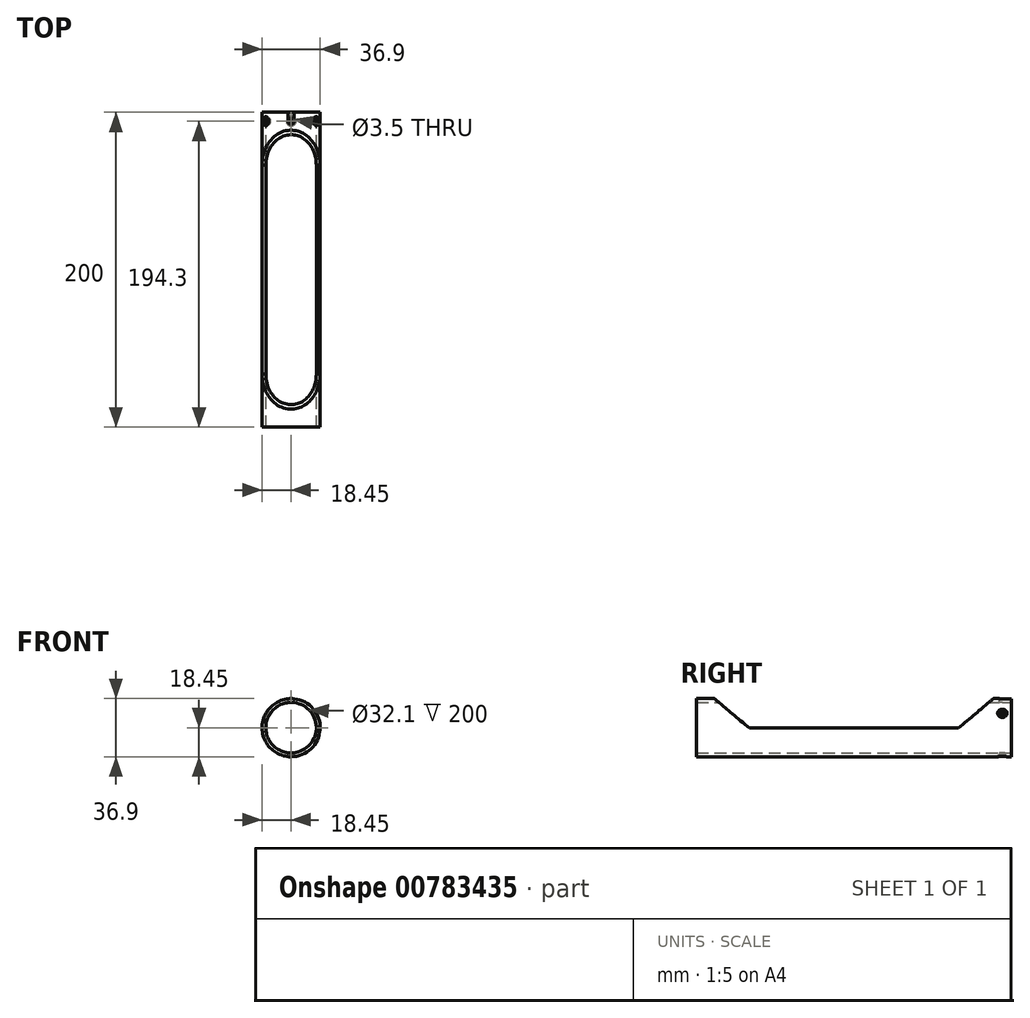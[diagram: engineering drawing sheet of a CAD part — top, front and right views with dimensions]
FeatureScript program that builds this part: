
annotation { "Feature Type Name" : "Feature", "Feature Type Description" : "" }
export const myFeature = defineFeature(function(context is Context, id is Id, definition is map)
    precondition{}
    {
        {
            var Q0;
            Q0=qCreatedBy(makeId("Front.planeOp"),FACE);
            var sketch = newSketch(context, id + "F0", { "sketchPlane" : qUnion([Q0])});
            skCircle(sketch, "E0", {"center": v(0, 0) * mm, "radius": 18.45 * mm});
            skCircle(sketch, "E1", {"center": v(0, 0) * mm, "radius": 16.05 * mm});
            skLineSegment(sketch, "E2.bottom", {"start": v(18.45, -18.45) * mm, "end": v(-18.45, -18.45) * mm});
            skLineSegment(sketch, "E2.top", {"start": v(18.45, 18.45) * mm, "end": v(-18.45, 18.45) * mm});
            skLineSegment(sketch, "E2.left", {"start": v(18.45, -18.45) * mm, "end": v(18.45, 18.45) * mm});
            skLineSegment(sketch, "E2.right", {"start": v(-18.45, -18.45) * mm, "end": v(-18.45, 18.45) * mm});
            skLineSegment(sketch, "E3", {"start": v(0, 0) * mm, "end": v(0, 18.45) * mm});
            skLineSegment(sketch, "E4", {"start": v(0, 0) * mm, "end": v(0, -18.45) * mm});
            skLineSegment(sketch, "E5", {"start": v(0, 0) * mm, "end": v(-15.98, 9.22) * mm});
            skLineSegment(sketch, "E6", {"start": v(0, 0) * mm, "end": v(15.98, 9.23) * mm});
            skSolve(sketch);
        }
        {
            var Q0;
            {var subQ3=sQuery(id+"F0.wireOp",EDGE,"CAZaTLFN-tJie-LHG7-8vTy-squ8jarRoMMn");var subQ5=sQuery(id+"F0.wireOp",EDGE,"E1");var subQ6=makeQuery(id+"F0.imprint","INTERSECT",VERTEX,{"derivedFrom":[subQ5,subQ3]});Q0=makeQuery(id+"F0.imprint","IMPRINT",FACE,{"disambiguationData":[TD([[makeQuery(id+"F0.imprint","IMPRINT",EDGE,{"disambiguationData":[TD([[subQ6,1.0]])],"derivedFrom":subQ5}),-1.0]])]});}
            var Q1;
            {var subQ3=sQuery(id+"F0.wireOp",EDGE,"CAZaTLFN-tJie-LHG7-8vTy-squ8jarRoMMn");var subQ5=sQuery(id+"F0.wireOp",EDGE,"E1");var subQ6=makeQuery(id+"F0.imprint","INTERSECT",VERTEX,{"derivedFrom":[subQ5,subQ3]});Q1=makeQuery(id+"F0.imprint","IMPRINT",FACE,{"disambiguationData":[TD([[makeQuery(id+"F0.imprint","IMPRINT",EDGE,{"disambiguationData":[TD([[subQ6,-1.0]])],"derivedFrom":subQ5}),-1.0]])]});}
            var Q2;
            {var subQ0=sQuery(id+"F0.wireOp",EDGE,"l8s0sOfb-fzFU-R0BE-n0NO-c75pVUIZOnGM");var subQ1=sQuery(id+"F0.wireOp",EDGE,"E0");var subQ2=makeQuery(id+"F0.imprint","INTERSECT",VERTEX,{"derivedFrom":[subQ1,subQ0]});Q2=makeQuery(id+"F0.imprint","IMPRINT",FACE,{"disambiguationData":[TD([[makeQuery(id+"F0.imprint","IMPRINT",EDGE,{"disambiguationData":[TD([[subQ2,1.0]])],"derivedFrom":subQ1}),1.0]])]});}
            var Q3;
            {var subQ0=sQuery(id+"F0.wireOp",EDGE,"4xxhsBqu-Dr4I-gKWc-ZI2R-gIkBFB4eemaq");var subQ1=sQuery(id+"F0.wireOp",EDGE,"E0");var subQ2=makeQuery(id+"F0.imprint","INTERSECT",VERTEX,{"derivedFrom":[subQ1,subQ0]});Q3=makeQuery(id+"F0.imprint","IMPRINT",FACE,{"disambiguationData":[TD([[makeQuery(id+"F0.imprint","IMPRINT",EDGE,{"disambiguationData":[TD([[subQ2,-1.0]])],"derivedFrom":subQ1}),1.0]])]});}
            var Q4;
            Q4=sQuery(id+"F0.wireOp",EDGE,"E0");
            extrude(context, id + "F1", {"entities" : qUnion([Q0, Q1, Q2, Q3]), "surfaceEntities" : qUnion([Q4]), "depth" : 100 * mm, "offsetDistance" : 25.4 * mm, "hasSecondDirection" : true, "secondDirectionOppositeDirection" : true, "secondDirectionDepth" : 100 * mm});
        }
        {
            var Q0;
            Q0=qCreatedBy(makeId("Right.planeOp"),FACE);
            var sketch = newSketch(context, id + "F2", { "sketchPlane" : qUnion([Q0])});
            skLineSegment(sketch, "E7.bottom", {"start": v(88.6, -0.25) * mm, "end": v(-88.6, -0.25) * mm});
            skLineSegment(sketch, "E7.top", {"start": v(88.6, 37.15) * mm, "end": v(-88.6, 37.15) * mm});
            skLineSegment(sketch, "E7.left", {"start": v(88.6, -0.25) * mm, "end": v(88.6, 37.15) * mm});
            skLineSegment(sketch, "E7.right", {"start": v(-88.6, -0.25) * mm, "end": v(-88.6, 37.15) * mm});
            skPoint(sketch, "E7.middle", {"position": v(0, 18.45) * mm});
            skLineSegment(sketch, "E8", {"start": v(-100, 18.45) * mm, "end": v(100, 18.45) * mm});
            skLineSegment(sketch, "E9", {"start": v(100, -18.45) * mm, "end": v(-100, -18.45) * mm});
            skLineSegment(sketch, "E10", {"start": v(88.6, 18.45) * mm, "end": v(66.31, -0.25) * mm});
            skLineSegment(sketch, "E11.MirrorCS", {"start": v(-88.6, 18.45) * mm, "end": v(-66.31, -0.25) * mm});
            skSolve(sketch);
        }
        {
            var Q0;
            {var subQ0=sQuery(id+"F2.wireOp",EDGE,"E7.top");Q0=makeQuery(id+"F2.imprint","IMPRINT",FACE,{"disambiguationData":[TD([[makeQuery(id+"F2.imprint","IMPRINT",EDGE,{"derivedFrom":subQ0}),1.0]])]});}
            var Q1;
            {var subQ0=sQuery(id+"F2.wireOp",EDGE,"E10");Q1=makeQuery(id+"F2.imprint","IMPRINT",FACE,{"disambiguationData":[TD([[makeQuery(id+"F2.imprint","IMPRINT",EDGE,{"derivedFrom":subQ0}),-1.0]])]});}
            extrude(context, id + "F3", {"entities" : qUnion([Q0, Q1]), "operationType" : NewBodyOperationType.REMOVE, "oppositeDirection" : true, "depth" : 50.8 * mm, "offsetDistance" : 25.4 * mm, "hasSecondDirection" : true, "secondDirectionOppositeDirection" : false, "secondDirectionDepth" : 50.8 * mm});
        }
        {
            var Q0;
            Q0=sQuery(id+"F0.wireOp",VERTEX,"E5.end");
            var Q1;
            Q1=sQuery(id+"F0.wireOp",EDGE,"E5");
            cPlane(context, id + "F4", {"entities" : qUnion([Q0, Q1]), "cplaneType" : CPlaneType.CURVE_POINT, "offset" : 25 * mm, "width" : 150 * mm, "height" : 150 * mm});
        }
        {
            var Q0;
            Q0=qCreatedBy(id+"F4.planeOp",FACE);
            var sketch = newSketch(context, id + "F5", { "sketchPlane" : qUnion([Q0])});
            skPoint(sketch, "E12", {"position": v(-94.3, 0) * mm});
            skPoint(sketch, "E13.MirrorP", {"position": v(94.3, 0) * mm});
            skSolve(sketch);
        }
        {
            var Q0;
            Q0=sQuery(id+"F5.wireOp",VERTEX,"E12");
            var Q1;
            Q1=makeQuery(id+"F1.opExtrude","SWEPT_BODY",BODY,{"disambiguationData":[OSD([sQuery(id+"F0.wireOp",EDGE,"E0"),sQuery(id+"F0.wireOp",EDGE,"E1")])]});
            hole(context, id + "F6", {"style" : HoleStyle.C_SINK, "endStyle" : HoleEndStyle.BLIND, "holeDiameter" : 3.5 * mm, "cSinkDiameter" : 6 * mm, "cSinkAngle" : 100 * degree, "majorDiameter" : 5 * mm, "holeDepth" : 5 * mm, "isTappedThrough" : true, "tappedDepth" : 12 * mm, "tapClearance" : 3, "locations" : qUnion([Q0]), "scope" : qUnion([Q1])});
        }
        {
            var Q0;
            Q0=sQuery(id+"F0.wireOp",VERTEX,"E6.end");
            var Q1;
            Q1=sQuery(id+"F0.wireOp",EDGE,"E6");
            cPlane(context, id + "F7", {"entities" : qUnion([Q0, Q1]), "cplaneType" : CPlaneType.CURVE_POINT, "offset" : 25 * mm, "width" : 150 * mm, "height" : 150 * mm});
        }
        {
            var Q0;
            Q0=qCreatedBy(id+"F7.planeOp",FACE);
            var sketch = newSketch(context, id + "F8", { "sketchPlane" : qUnion([Q0])});
            skPoint(sketch, "E14", {"position": v(94.3, 0) * mm});
            skSolve(sketch);
        }
        {
            var Q0;
            Q0=sQuery(id+"F8.wireOp",VERTEX,"E14");
            var Q1;
            Q1=makeQuery(id+"F1.opExtrude","SWEPT_BODY",BODY,{"disambiguationData":[OSD([sQuery(id+"F0.wireOp",EDGE,"E0"),sQuery(id+"F0.wireOp",EDGE,"E1")])]});
            hole(context, id + "F9", {"style" : HoleStyle.C_SINK, "endStyle" : HoleEndStyle.BLIND, "holeDiameter" : 3.5 * mm, "cSinkDiameter" : 6 * mm, "cSinkAngle" : 100 * degree, "majorDiameter" : 5 * mm, "holeDepth" : 5 * mm, "isTappedThrough" : true, "tappedDepth" : 12 * mm, "tapClearance" : 3, "locations" : qUnion([Q0]), "scope" : qUnion([Q1])});
        }
        {
            var Q0;
            Q0=sQuery(id+"F0.wireOp",VERTEX,"E3.end");
            var Q1;
            Q1=sQuery(id+"F0.wireOp",EDGE,"E3");
            cPlane(context, id + "F10", {"entities" : qUnion([Q0, Q1]), "cplaneType" : CPlaneType.CURVE_POINT, "offset" : 25 * mm, "width" : 150 * mm, "height" : 150 * mm});
        }
        {
            var Q0;
            Q0=qCreatedBy(id+"F10.planeOp",FACE);
            var sketch = newSketch(context, id + "F11", { "sketchPlane" : qUnion([Q0])});
            skCircle(sketch, "E15", {"center": v(0, 94.3) * mm, "radius": 2 * mm});
            skLineSegment(sketch, "E16", {"start": v(2, 94.3) * mm, "end": v(2, 100) * mm});
            skLineSegment(sketch, "E17", {"start": v(-2, 94.3) * mm, "end": v(-2, 100) * mm});
            skLineSegment(sketch, "E18", {"start": v(-2, 100) * mm, "end": v(2, 100) * mm});
            skLineSegment(sketch, "E19.0", {"start": v(18.45, 100) * mm, "end": v(-18.45, 100) * mm});
            skSolve(sketch);
        }
        {
            var Q0;
            {var subQ0=sQuery(id+"F11.wireOp",EDGE,"E16");Q0=makeQuery(id+"F11.imprint","IMPRINT",FACE,{"disambiguationData":[TD([[makeQuery(id+"F11.imprint","IMPRINT",EDGE,{"derivedFrom":subQ0}),1.0]])]});}
            var Q1;
            {var subQ0=sQuery(id+"F11.wireOp",EDGE,"E15");var subQ1=makeQuery(id+"F11.imprint","INTERSECT",VERTEX,{"derivedFrom":[subQ0,sQuery(id+"F11.wireOp",EDGE,"E16")]});Q1=makeQuery(id+"F11.imprint","IMPRINT",FACE,{"disambiguationData":[TD([[makeQuery(id+"F11.imprint","IMPRINT",EDGE,{"disambiguationData":[TD([[subQ1,-1.0]])],"derivedFrom":subQ0}),1.0]])]});}
            extrude(context, id + "F12", {"entities" : qUnion([Q0, Q1]), "operationType" : NewBodyOperationType.REMOVE, "oppositeDirection" : true, "depth" : 19.1 * mm, "offsetDistance" : 25 * mm});
        }
        {
            var Q0;
            Q0=sQuery(id+"F0.wireOp",EDGE,"E2.bottom");
            cPoint(context, id + "F13", {"entities" : qUnion([Q0]), "parameter" : 0.5});
        }
        {
            var Q0;
            Q0 = qCreatedBy(id + "F13" ,VERTEX);
            var Q1;
            Q1=sQuery(id+"F0.wireOp",EDGE,"E4");
            cPlane(context, id + "F14", {"entities" : qUnion([Q0, Q1]), "cplaneType" : CPlaneType.CURVE_POINT, "offset" : 25 * mm, "width" : 150 * mm, "height" : 150 * mm});
        }
        {
            var Q0;
            Q0=qCreatedBy(id+"F14.planeOp",FACE);
            var sketch = newSketch(context, id + "F15", { "sketchPlane" : qUnion([Q0])});
            skPoint(sketch, "E20", {"position": v(0, -94.3) * mm});
            skSolve(sketch);
        }
        {
            var Q0;
            Q0=sQuery(id+"F15.wireOp",VERTEX,"E20");
            var Q1;
            Q1=makeQuery(id+"F1.opExtrude","SWEPT_BODY",BODY,{"disambiguationData":[OSD([sQuery(id+"F0.wireOp",EDGE,"E0"),sQuery(id+"F0.wireOp",EDGE,"E1")])]});
            hole(context, id + "F16", {"style" : HoleStyle.C_SINK, "endStyle" : HoleEndStyle.BLIND, "holeDiameter" : 3.5 * mm, "cSinkDiameter" : 6 * mm, "cSinkAngle" : 100 * degree, "majorDiameter" : 5 * mm, "holeDepth" : 5 * mm, "isTappedThrough" : true, "tappedDepth" : 12 * mm, "tapClearance" : 3, "locations" : qUnion([Q0]), "scope" : qUnion([Q1])});
        }
    });
